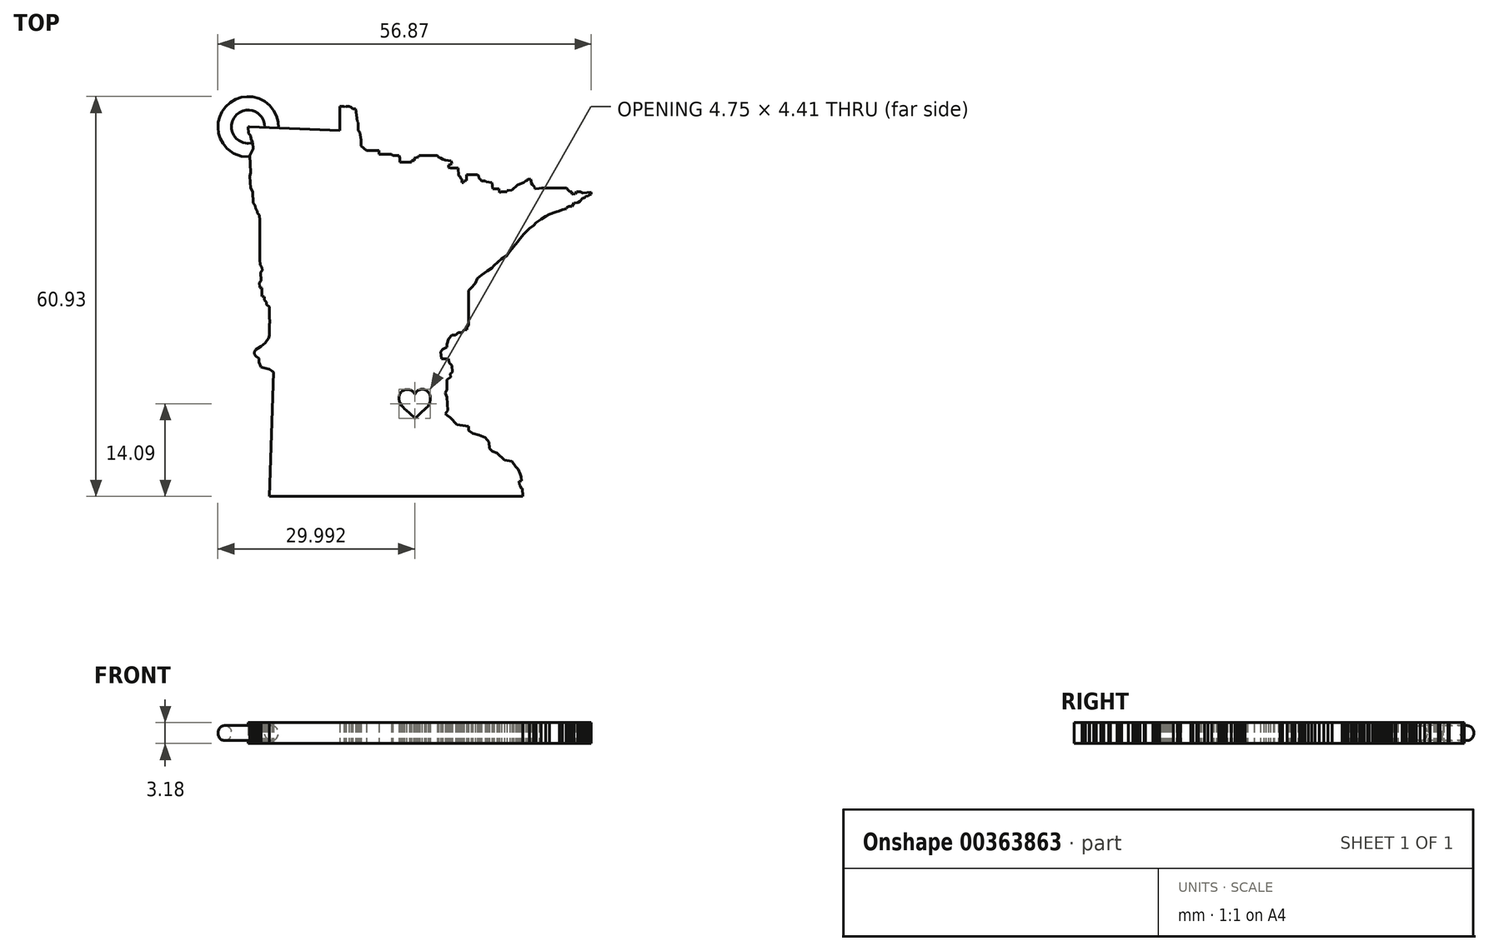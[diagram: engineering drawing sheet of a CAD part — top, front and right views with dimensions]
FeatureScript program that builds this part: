
annotation { "Feature Type Name" : "Feature", "Feature Type Description" : "" }
export const myFeature = defineFeature(function(context is Context, id is Id, definition is map)
    precondition{}
    {
        {
            var Q0;
            Q0=qCreatedBy(makeId("Top.planeOp"),FACE);
            var sketch = newSketch(context, id + "F0", { "sketchPlane" : qUnion([Q0])});
            skLineSegment(sketch, "E0", {"start": v(12.03, -4) * mm, "end": v(25.82, -4.56) * mm});
            skLineSegment(sketch, "E1", {"start": v(25.82, -4.56) * mm, "end": v(25.82, -1.03) * mm});
            skLineSegment(sketch, "E2", {"start": v(25.82, -1.03) * mm, "end": v(25.82, -0.87) * mm});
            skLineSegment(sketch, "E3", {"start": v(25.82, -0.87) * mm, "end": v(26.23, -0.87) * mm});
            skLineSegment(sketch, "E4", {"start": v(26.23, -0.87) * mm, "end": v(26.44, -0.87) * mm});
            skLineSegment(sketch, "E5", {"start": v(26.44, -0.87) * mm, "end": v(26.65, -1.03) * mm});
            skLineSegment(sketch, "E6", {"start": v(26.65, -1.03) * mm, "end": v(26.78, -0.87) * mm});
            skLineSegment(sketch, "E7", {"start": v(26.78, -0.87) * mm, "end": v(27.2, -0.87) * mm});
            skLineSegment(sketch, "E8", {"start": v(27.2, -0.87) * mm, "end": v(27.55, -1.03) * mm});
            skLineSegment(sketch, "E9", {"start": v(27.55, -1.03) * mm, "end": v(27.82, -1.25) * mm});
            skLineSegment(sketch, "E10", {"start": v(27.82, -1.25) * mm, "end": v(28.24, -1.25) * mm});
            skLineSegment(sketch, "E11", {"start": v(28.24, -1.25) * mm, "end": v(28.47, -3.17) * mm});
            skLineSegment(sketch, "E12", {"start": v(28.47, -3.17) * mm, "end": v(28.63, -3.36) * mm});
            skLineSegment(sketch, "E13", {"start": v(28.63, -3.36) * mm, "end": v(28.63, -4.56) * mm});
            skLineSegment(sketch, "E14", {"start": v(28.63, -4.56) * mm, "end": v(28.86, -4.8) * mm});
            skLineSegment(sketch, "E15", {"start": v(28.86, -4.8) * mm, "end": v(29.07, -6.06) * mm});
            skLineSegment(sketch, "E16", {"start": v(29.07, -6.06) * mm, "end": v(29.07, -6.64) * mm});
            skLineSegment(sketch, "E17", {"start": v(29.07, -6.64) * mm, "end": v(29.07, -6.94) * mm});
            skLineSegment(sketch, "E18", {"start": v(29.07, -6.94) * mm, "end": v(29.91, -7.6) * mm});
            skLineSegment(sketch, "E19", {"start": v(29.91, -7.6) * mm, "end": v(31.81, -7.6) * mm});
            skLineSegment(sketch, "E20", {"start": v(31.81, -7.6) * mm, "end": v(31.81, -8.21) * mm});
            skLineSegment(sketch, "E21", {"start": v(31.81, -8.21) * mm, "end": v(33.7, -8.21) * mm});
            skLineSegment(sketch, "E22", {"start": v(33.7, -8.21) * mm, "end": v(33.87, -8.4) * mm});
            skLineSegment(sketch, "E23", {"start": v(33.87, -8.4) * mm, "end": v(34.84, -8.4) * mm});
            skLineSegment(sketch, "E24", {"start": v(34.84, -8.4) * mm, "end": v(35, -8.76) * mm});
            skLineSegment(sketch, "E25", {"start": v(35, -8.76) * mm, "end": v(35, -9.4) * mm});
            skLineSegment(sketch, "E26", {"start": v(35, -9.4) * mm, "end": v(36.75, -9.4) * mm});
            skLineSegment(sketch, "E27", {"start": v(36.75, -9.4) * mm, "end": v(36.75, -9.16) * mm});
            skLineSegment(sketch, "E28", {"start": v(36.75, -9.16) * mm, "end": v(37.17, -9.16) * mm});
            skLineSegment(sketch, "E29", {"start": v(37.17, -9.16) * mm, "end": v(37.17, -8.76) * mm});
            skLineSegment(sketch, "E30", {"start": v(37.17, -8.76) * mm, "end": v(37.77, -8.64) * mm});
            skLineSegment(sketch, "E31", {"start": v(37.77, -8.64) * mm, "end": v(37.9, -8.4) * mm});
            skLineSegment(sketch, "E32", {"start": v(37.9, -8.4) * mm, "end": v(39.55, -8.4) * mm});
            skLineSegment(sketch, "E33", {"start": v(39.55, -8.4) * mm, "end": v(40.68, -8.4) * mm});
            skLineSegment(sketch, "E34", {"start": v(40.68, -8.4) * mm, "end": v(40.9, -8.63) * mm});
            skLineSegment(sketch, "E35", {"start": v(40.9, -8.63) * mm, "end": v(41.2, -8.76) * mm});
            skLineSegment(sketch, "E36", {"start": v(41.2, -8.76) * mm, "end": v(41.49, -8.96) * mm});
            skLineSegment(sketch, "E37", {"start": v(41.49, -8.96) * mm, "end": v(41.87, -9.1) * mm});
            skLineSegment(sketch, "E38", {"start": v(41.87, -9.1) * mm, "end": v(42.76, -9.21) * mm});
            skLineSegment(sketch, "E39", {"start": v(42.76, -9.21) * mm, "end": v(42.9, -9.68) * mm});
            skLineSegment(sketch, "E40", {"start": v(42.9, -9.68) * mm, "end": v(42.4, -9.84) * mm});
            skLineSegment(sketch, "E41", {"start": v(42.4, -9.84) * mm, "end": v(42.4, -10.23) * mm});
            skLineSegment(sketch, "E42", {"start": v(42.4, -10.23) * mm, "end": v(42.7, -10.31) * mm});
            skLineSegment(sketch, "E43", {"start": v(42.7, -10.31) * mm, "end": v(43.03, -10.31) * mm});
            skLineSegment(sketch, "E44", {"start": v(43.03, -10.31) * mm, "end": v(43.87, -10.31) * mm});
            skLineSegment(sketch, "E45", {"start": v(43.87, -10.31) * mm, "end": v(43.95, -11.46) * mm});
            skLineSegment(sketch, "E46", {"start": v(43.95, -11.46) * mm, "end": v(44.17, -11.61) * mm});
            skLineSegment(sketch, "E47", {"start": v(44.17, -11.61) * mm, "end": v(44.27, -11.9) * mm});
            skLineSegment(sketch, "E48", {"start": v(44.27, -11.9) * mm, "end": v(44.43, -12.04) * mm});
            skLineSegment(sketch, "E49", {"start": v(44.43, -12.04) * mm, "end": v(44.46, -12.5) * mm});
            skLineSegment(sketch, "E50", {"start": v(44.46, -12.5) * mm, "end": v(44.7, -12.5) * mm});
            skLineSegment(sketch, "E51", {"start": v(44.7, -12.5) * mm, "end": v(44.77, -12.25) * mm});
            skLineSegment(sketch, "E52", {"start": v(44.77, -12.25) * mm, "end": v(45.11, -12.22) * mm});
            skLineSegment(sketch, "E53", {"start": v(45.11, -12.22) * mm, "end": v(45.11, -11.28) * mm});
            skLineSegment(sketch, "E54", {"start": v(45.11, -11.28) * mm, "end": v(46.8, -11.28) * mm});
            skLineSegment(sketch, "E55", {"start": v(46.8, -11.28) * mm, "end": v(47, -11.44) * mm});
            skLineSegment(sketch, "E56", {"start": v(47, -11.44) * mm, "end": v(47.03, -11.9) * mm});
            skLineSegment(sketch, "E57", {"start": v(47.03, -11.9) * mm, "end": v(47.24, -12.04) * mm});
            skLineSegment(sketch, "E58", {"start": v(47.24, -12.04) * mm, "end": v(47.42, -12.27) * mm});
            skLineSegment(sketch, "E59", {"start": v(47.42, -12.27) * mm, "end": v(47.96, -12.23) * mm});
            skLineSegment(sketch, "E60", {"start": v(47.96, -12.23) * mm, "end": v(48.1, -12.42) * mm});
            skLineSegment(sketch, "E61", {"start": v(48.1, -12.42) * mm, "end": v(48.99, -12.51) * mm});
            skLineSegment(sketch, "E62", {"start": v(48.99, -12.51) * mm, "end": v(49.15, -13.49) * mm});
            skLineSegment(sketch, "E63", {"start": v(49.15, -13.49) * mm, "end": v(50.1, -13.49) * mm});
            skLineSegment(sketch, "E64", {"start": v(50.1, -13.49) * mm, "end": v(50.13, -14.05) * mm});
            skLineSegment(sketch, "E65", {"start": v(50.13, -14.05) * mm, "end": v(50.45, -13.93) * mm});
            skLineSegment(sketch, "E66", {"start": v(50.45, -13.93) * mm, "end": v(51.27, -13.93) * mm});
            skLineSegment(sketch, "E67", {"start": v(51.27, -13.93) * mm, "end": v(51.27, -13.73) * mm});
            skLineSegment(sketch, "E68", {"start": v(51.27, -13.73) * mm, "end": v(52.04, -13.68) * mm});
            skLineSegment(sketch, "E69", {"start": v(52.04, -13.68) * mm, "end": v(52.9, -12.9) * mm});
            skLineSegment(sketch, "E70", {"start": v(52.9, -12.9) * mm, "end": v(53.3, -12.73) * mm});
            skLineSegment(sketch, "E71", {"start": v(53.3, -12.73) * mm, "end": v(53.81, -12.52) * mm});
            skLineSegment(sketch, "E72", {"start": v(53.81, -12.52) * mm, "end": v(54.14, -12.23) * mm});
            skLineSegment(sketch, "E73", {"start": v(54.14, -12.23) * mm, "end": v(54.34, -12.22) * mm});
            skLineSegment(sketch, "E74", {"start": v(54.34, -12.22) * mm, "end": v(54.48, -12.04) * mm});
            skLineSegment(sketch, "E75", {"start": v(54.48, -12.04) * mm, "end": v(54.88, -12) * mm});
            skLineSegment(sketch, "E76", {"start": v(54.88, -12) * mm, "end": v(54.98, -12.23) * mm});
            skLineSegment(sketch, "E77", {"start": v(54.98, -12.23) * mm, "end": v(55, -12.52) * mm});
            skLineSegment(sketch, "E78", {"start": v(55, -12.52) * mm, "end": v(55.15, -12.81) * mm});
            skLineSegment(sketch, "E79", {"start": v(55.15, -12.81) * mm, "end": v(55.37, -13.04) * mm});
            skLineSegment(sketch, "E80", {"start": v(55.37, -13.04) * mm, "end": v(55.52, -13.3) * mm});
            skLineSegment(sketch, "E81", {"start": v(55.52, -13.3) * mm, "end": v(55.53, -13.47) * mm});
            skLineSegment(sketch, "E82", {"start": v(55.53, -13.47) * mm, "end": v(56.2, -13.43) * mm});
            skLineSegment(sketch, "E83", {"start": v(56.2, -13.43) * mm, "end": v(56.59, -13.3) * mm});
            skLineSegment(sketch, "E84", {"start": v(56.59, -13.3) * mm, "end": v(59.44, -13.3) * mm});
            skLineSegment(sketch, "E85", {"start": v(59.44, -13.3) * mm, "end": v(60.4, -13.3) * mm});
            skLineSegment(sketch, "E86", {"start": v(60.4, -13.3) * mm, "end": v(60.62, -13.68) * mm});
            skLineSegment(sketch, "E87", {"start": v(60.62, -13.68) * mm, "end": v(60.85, -13.93) * mm});
            skLineSegment(sketch, "E88", {"start": v(60.85, -13.93) * mm, "end": v(61.17, -13.93) * mm});
            skLineSegment(sketch, "E89", {"start": v(61.17, -13.93) * mm, "end": v(61.2, -14.28) * mm});
            skLineSegment(sketch, "E90", {"start": v(61.2, -14.28) * mm, "end": v(61.68, -14.24) * mm});
            skLineSegment(sketch, "E91", {"start": v(61.68, -14.24) * mm, "end": v(61.91, -13.93) * mm});
            skLineSegment(sketch, "E92", {"start": v(61.91, -13.93) * mm, "end": v(62.46, -13.9) * mm});
            skLineSegment(sketch, "E93", {"start": v(62.46, -13.9) * mm, "end": v(62.85, -14.1) * mm});
            skLineSegment(sketch, "E94", {"start": v(62.85, -14.1) * mm, "end": v(63.82, -14.03) * mm});
            skLineSegment(sketch, "E95", {"start": v(63.82, -14.03) * mm, "end": v(64.1, -14) * mm});
            skLineSegment(sketch, "E96", {"start": v(64.1, -14) * mm, "end": v(64.12, -14.27) * mm});
            skLineSegment(sketch, "E97", {"start": v(64.12, -14.27) * mm, "end": v(63.82, -14.43) * mm});
            skLineSegment(sketch, "E98", {"start": v(63.82, -14.43) * mm, "end": v(63.68, -14.57) * mm});
            skLineSegment(sketch, "E99", {"start": v(63.68, -14.57) * mm, "end": v(63.32, -14.6) * mm});
            skLineSegment(sketch, "E100", {"start": v(63.32, -14.6) * mm, "end": v(63.12, -14.85) * mm});
            skLineSegment(sketch, "E101", {"start": v(63.12, -14.85) * mm, "end": v(62.83, -14.87) * mm});
            skLineSegment(sketch, "E102", {"start": v(62.83, -14.87) * mm, "end": v(62.38, -15.38) * mm});
            skLineSegment(sketch, "E103", {"start": v(62.38, -15.38) * mm, "end": v(62.1, -15.56) * mm});
            skLineSegment(sketch, "E104", {"start": v(62.1, -15.56) * mm, "end": v(61.52, -15.6) * mm});
            skLineSegment(sketch, "E105", {"start": v(61.52, -15.6) * mm, "end": v(61.17, -16.11) * mm});
            skLineSegment(sketch, "E106", {"start": v(61.17, -16.11) * mm, "end": v(60.75, -16.14) * mm});
            skLineSegment(sketch, "E107", {"start": v(60.75, -16.14) * mm, "end": v(60.4, -16.33) * mm});
            skLineSegment(sketch, "E108", {"start": v(60.4, -16.33) * mm, "end": v(60.3, -16.51) * mm});
            skLineSegment(sketch, "E109", {"start": v(60.3, -16.51) * mm, "end": v(59.73, -16.62) * mm});
            skLineSegment(sketch, "E110", {"start": v(59.73, -16.62) * mm, "end": v(59.27, -16.82) * mm});
            skLineSegment(sketch, "E111", {"start": v(59.27, -16.82) * mm, "end": v(58.63, -17.05) * mm});
            skLineSegment(sketch, "E112", {"start": v(58.63, -17.05) * mm, "end": v(57.77, -17.34) * mm});
            skLineSegment(sketch, "E113", {"start": v(57.77, -17.34) * mm, "end": v(57.18, -17.65) * mm});
            skLineSegment(sketch, "E114", {"start": v(57.18, -17.65) * mm, "end": v(56.52, -18.07) * mm});
            skLineSegment(sketch, "E115", {"start": v(56.52, -18.07) * mm, "end": v(55.76, -18.61) * mm});
            skLineSegment(sketch, "E116", {"start": v(55.76, -18.61) * mm, "end": v(55.37, -19.05) * mm});
            skLineSegment(sketch, "E117", {"start": v(55.37, -19.05) * mm, "end": v(54.7, -19.5) * mm});
            skLineSegment(sketch, "E118", {"start": v(54.7, -19.5) * mm, "end": v(53.83, -20.42) * mm});
            skLineSegment(sketch, "E119", {"start": v(53.83, -20.42) * mm, "end": v(53.3, -21) * mm});
            skLineSegment(sketch, "E120", {"start": v(53.3, -21) * mm, "end": v(52.88, -21.62) * mm});
            skLineSegment(sketch, "E121", {"start": v(52.88, -21.62) * mm, "end": v(52.33, -22.3) * mm});
            skLineSegment(sketch, "E122", {"start": v(52.33, -22.3) * mm, "end": v(51.71, -23) * mm});
            skLineSegment(sketch, "E123", {"start": v(51.71, -23) * mm, "end": v(51.27, -23.65) * mm});
            skLineSegment(sketch, "E124", {"start": v(51.27, -23.65) * mm, "end": v(50.45, -24.14) * mm});
            skLineSegment(sketch, "E125", {"start": v(50.45, -24.14) * mm, "end": v(49.9, -24.66) * mm});
            skLineSegment(sketch, "E126", {"start": v(49.9, -24.66) * mm, "end": v(49.31, -25.12) * mm});
            skLineSegment(sketch, "E127", {"start": v(49.31, -25.12) * mm, "end": v(49, -25.55) * mm});
            skLineSegment(sketch, "E128", {"start": v(49, -25.55) * mm, "end": v(48.3, -25.98) * mm});
            skLineSegment(sketch, "E129", {"start": v(48.3, -25.98) * mm, "end": v(47.44, -26.63) * mm});
            skLineSegment(sketch, "E130", {"start": v(47.44, -26.63) * mm, "end": v(46.8, -27.12) * mm});
            skLineSegment(sketch, "E131", {"start": v(46.8, -27.12) * mm, "end": v(46.45, -27.89) * mm});
            skLineSegment(sketch, "E132", {"start": v(46.45, -27.89) * mm, "end": v(45.8, -28.6) * mm});
            skLineSegment(sketch, "E133", {"start": v(45.8, -28.6) * mm, "end": v(45.47, -28.93) * mm});
            skLineSegment(sketch, "E134", {"start": v(45.47, -28.93) * mm, "end": v(45.47, -34.3) * mm});
            skLineSegment(sketch, "E135", {"start": v(45.47, -34.3) * mm, "end": v(45.19, -34.55) * mm});
            skLineSegment(sketch, "E136", {"start": v(45.19, -34.55) * mm, "end": v(45.21, -34.96) * mm});
            skLineSegment(sketch, "E137", {"start": v(45.21, -34.96) * mm, "end": v(44.74, -35) * mm});
            skLineSegment(sketch, "E138", {"start": v(44.74, -35) * mm, "end": v(44.43, -35.36) * mm});
            skLineSegment(sketch, "E139", {"start": v(44.43, -35.36) * mm, "end": v(43.87, -35.4) * mm});
            skLineSegment(sketch, "E140", {"start": v(43.87, -35.4) * mm, "end": v(43.5, -35.74) * mm});
            skLineSegment(sketch, "E141", {"start": v(43.5, -35.74) * mm, "end": v(42.9, -35.78) * mm});
            skLineSegment(sketch, "E142", {"start": v(42.9, -35.78) * mm, "end": v(42.4, -36.35) * mm});
            skLineSegment(sketch, "E143", {"start": v(42.4, -36.35) * mm, "end": v(42.14, -37.13) * mm});
            skLineSegment(sketch, "E144", {"start": v(42.14, -37.13) * mm, "end": v(42.17, -37.61) * mm});
            skLineSegment(sketch, "E145", {"start": v(42.17, -37.61) * mm, "end": v(41.49, -37.93) * mm});
            skLineSegment(sketch, "E146", {"start": v(41.49, -37.93) * mm, "end": v(41.23, -38.3) * mm});
            skLineSegment(sketch, "E147", {"start": v(41.23, -38.3) * mm, "end": v(41.28, -39.01) * mm});
            skLineSegment(sketch, "E148", {"start": v(41.28, -39.01) * mm, "end": v(41.3, -39.4) * mm});
            skLineSegment(sketch, "E149", {"start": v(41.3, -39.4) * mm, "end": v(42.4, -39.4) * mm});
            skLineSegment(sketch, "E150", {"start": v(42.4, -39.4) * mm, "end": v(42.45, -39.96) * mm});
            skLineSegment(sketch, "E151", {"start": v(42.45, -39.96) * mm, "end": v(42.9, -40.42) * mm});
            skLineSegment(sketch, "E152", {"start": v(42.9, -40.42) * mm, "end": v(42.94, -40.94) * mm});
            skLineSegment(sketch, "E153", {"start": v(42.94, -40.94) * mm, "end": v(42.97, -41.41) * mm});
            skLineSegment(sketch, "E154", {"start": v(42.97, -41.41) * mm, "end": v(42.68, -41.63) * mm});
            skLineSegment(sketch, "E155", {"start": v(42.68, -41.63) * mm, "end": v(42.72, -42.2) * mm});
            skLineSegment(sketch, "E156", {"start": v(42.72, -42.2) * mm, "end": v(42.17, -42.55) * mm});
            skLineSegment(sketch, "E157", {"start": v(42.17, -42.55) * mm, "end": v(42.17, -44.1) * mm});
            skLineSegment(sketch, "E158", {"start": v(42.17, -44.1) * mm, "end": v(41.87, -44.55) * mm});
            skLineSegment(sketch, "E159", {"start": v(41.87, -44.55) * mm, "end": v(42.12, -45.2) * mm});
            skLineSegment(sketch, "E160", {"start": v(42.12, -45.2) * mm, "end": v(42.16, -45.83) * mm});
            skLineSegment(sketch, "E161", {"start": v(42.16, -45.83) * mm, "end": v(42.21, -46.63) * mm});
            skLineSegment(sketch, "E162", {"start": v(42.21, -46.63) * mm, "end": v(42.26, -47.28) * mm});
            skLineSegment(sketch, "E163", {"start": v(42.26, -47.28) * mm, "end": v(41.87, -47.75) * mm});
            skLineSegment(sketch, "E164", {"start": v(41.87, -47.75) * mm, "end": v(42.21, -48.03) * mm});
            skLineSegment(sketch, "E165", {"start": v(42.21, -48.03) * mm, "end": v(42.64, -48.3) * mm});
            skLineSegment(sketch, "E166", {"start": v(42.64, -48.3) * mm, "end": v(43.67, -49.43) * mm});
            skLineSegment(sketch, "E167", {"start": v(43.67, -49.43) * mm, "end": v(45.42, -49.65) * mm});
            skLineSegment(sketch, "E168", {"start": v(45.42, -49.65) * mm, "end": v(45.46, -50.3) * mm});
            skLineSegment(sketch, "E169", {"start": v(45.46, -50.3) * mm, "end": v(46.1, -50.73) * mm});
            skLineSegment(sketch, "E170", {"start": v(46.1, -50.73) * mm, "end": v(47.01, -51) * mm});
            skLineSegment(sketch, "E171", {"start": v(47.01, -51) * mm, "end": v(47.96, -51.4) * mm});
            skLineSegment(sketch, "E172", {"start": v(47.96, -51.4) * mm, "end": v(48.56, -52.06) * mm});
            skLineSegment(sketch, "E173", {"start": v(48.56, -52.06) * mm, "end": v(48.6, -52.65) * mm});
            skLineSegment(sketch, "E174", {"start": v(48.6, -52.65) * mm, "end": v(48.63, -53.05) * mm});
            skLineSegment(sketch, "E175", {"start": v(48.63, -53.05) * mm, "end": v(49.09, -53.47) * mm});
            skLineSegment(sketch, "E176", {"start": v(49.09, -53.47) * mm, "end": v(49.8, -53.75) * mm});
            skLineSegment(sketch, "E177", {"start": v(49.8, -53.75) * mm, "end": v(50.92, -54.8) * mm});
            skLineSegment(sketch, "E178", {"start": v(50.92, -54.8) * mm, "end": v(52.04, -55.02) * mm});
            skLineSegment(sketch, "E179", {"start": v(52.04, -55.02) * mm, "end": v(52.64, -55.8) * mm});
            skLineSegment(sketch, "E180", {"start": v(52.64, -55.8) * mm, "end": v(53, -56.22) * mm});
            skLineSegment(sketch, "E181", {"start": v(53, -56.22) * mm, "end": v(53.3, -56.98) * mm});
            skLineSegment(sketch, "E182", {"start": v(53.3, -56.98) * mm, "end": v(53.47, -57.32) * mm});
            skLineSegment(sketch, "E183", {"start": v(53.47, -57.32) * mm, "end": v(53.51, -58) * mm});
            skLineSegment(sketch, "E184", {"start": v(53.51, -58) * mm, "end": v(53.14, -58.02) * mm});
            skLineSegment(sketch, "E185", {"start": v(53.14, -58.02) * mm, "end": v(53.18, -58.58) * mm});
            skLineSegment(sketch, "E186", {"start": v(53.18, -58.58) * mm, "end": v(53.3, -58.76) * mm});
            skLineSegment(sketch, "E187", {"start": v(53.3, -58.76) * mm, "end": v(53.49, -59.18) * mm});
            skLineSegment(sketch, "E188", {"start": v(53.49, -59.18) * mm, "end": v(53.62, -59.11) * mm});
            skLineSegment(sketch, "E189", {"start": v(53.62, -59.11) * mm, "end": v(53.69, -60.12) * mm});
            skLineSegment(sketch, "E190", {"start": v(53.69, -60.12) * mm, "end": v(53.7, -60.33) * mm});
            skLineSegment(sketch, "E191", {"start": v(53.7, -60.33) * mm, "end": v(15.07, -60.33) * mm});
            skLineSegment(sketch, "E192", {"start": v(15.07, -60.33) * mm, "end": v(15.7, -41.41) * mm});
            skLineSegment(sketch, "E193", {"start": v(15.7, -41.41) * mm, "end": v(15.5, -41.2) * mm});
            skLineSegment(sketch, "E194", {"start": v(15.5, -41.2) * mm, "end": v(15.08, -40.95) * mm});
            skLineSegment(sketch, "E195", {"start": v(15.08, -40.95) * mm, "end": v(14.34, -40.76) * mm});
            skLineSegment(sketch, "E196", {"start": v(14.34, -40.76) * mm, "end": v(13.8, -40.62) * mm});
            skLineSegment(sketch, "E197", {"start": v(13.8, -40.62) * mm, "end": v(13.52, -39.9) * mm});
            skLineSegment(sketch, "E198", {"start": v(13.52, -39.9) * mm, "end": v(13.5, -39.58) * mm});
            skLineSegment(sketch, "E199", {"start": v(13.5, -39.58) * mm, "end": v(13.48, -39.31) * mm});
            skLineSegment(sketch, "E200", {"start": v(13.48, -39.31) * mm, "end": v(13.1, -39.01) * mm});
            skLineSegment(sketch, "E201", {"start": v(13.1, -39.01) * mm, "end": v(12.84, -38.69) * mm});
            skLineSegment(sketch, "E202", {"start": v(12.84, -38.69) * mm, "end": v(12.81, -38.33) * mm});
            skLineSegment(sketch, "E203", {"start": v(12.81, -38.33) * mm, "end": v(13.03, -37.99) * mm});
            skLineSegment(sketch, "E204", {"start": v(13.03, -37.99) * mm, "end": v(13.32, -37.77) * mm});
            skLineSegment(sketch, "E205", {"start": v(13.32, -37.77) * mm, "end": v(13.84, -37.46) * mm});
            skLineSegment(sketch, "E206", {"start": v(13.84, -37.46) * mm, "end": v(14.14, -37.2) * mm});
            skLineSegment(sketch, "E207", {"start": v(14.14, -37.2) * mm, "end": v(14.47, -36.94) * mm});
            skLineSegment(sketch, "E208", {"start": v(14.47, -36.94) * mm, "end": v(14.7, -36.58) * mm});
            skLineSegment(sketch, "E209", {"start": v(14.7, -36.58) * mm, "end": v(14.99, -36.24) * mm});
            skLineSegment(sketch, "E210", {"start": v(14.99, -36.24) * mm, "end": v(15.1, -35.82) * mm});
            skLineSegment(sketch, "E211", {"start": v(15.1, -35.82) * mm, "end": v(15.1, -34.13) * mm});
            skLineSegment(sketch, "E212", {"start": v(15.1, -34.13) * mm, "end": v(15.16, -33.88) * mm});
            skLineSegment(sketch, "E213", {"start": v(15.16, -33.88) * mm, "end": v(15.15, -33.7) * mm});
            skLineSegment(sketch, "E214", {"start": v(15.15, -33.7) * mm, "end": v(15.12, -33.3) * mm});
            skLineSegment(sketch, "E215", {"start": v(15.12, -33.3) * mm, "end": v(15.1, -32.89) * mm});
            skLineSegment(sketch, "E216", {"start": v(15.1, -32.89) * mm, "end": v(15.1, -31.93) * mm});
            skLineSegment(sketch, "E217", {"start": v(15.1, -31.93) * mm, "end": v(15.06, -31.43) * mm});
            skLineSegment(sketch, "E218", {"start": v(15.06, -31.43) * mm, "end": v(14.66, -31.12) * mm});
            skLineSegment(sketch, "E219", {"start": v(14.66, -31.12) * mm, "end": v(14.63, -30.73) * mm});
            skLineSegment(sketch, "E220", {"start": v(14.63, -30.73) * mm, "end": v(14.34, -30.4) * mm});
            skLineSegment(sketch, "E221", {"start": v(14.34, -30.4) * mm, "end": v(14.31, -29.94) * mm});
            skLineSegment(sketch, "E222", {"start": v(14.31, -29.94) * mm, "end": v(13.97, -29.85) * mm});
            skLineSegment(sketch, "E223", {"start": v(13.97, -29.85) * mm, "end": v(13.97, -29.2) * mm});
            skLineSegment(sketch, "E224", {"start": v(13.97, -29.2) * mm, "end": v(13.93, -28.6) * mm});
            skLineSegment(sketch, "E225", {"start": v(13.93, -28.6) * mm, "end": v(13.65, -28.52) * mm});
            skLineSegment(sketch, "E226", {"start": v(13.65, -28.52) * mm, "end": v(13.6, -27.74) * mm});
            skLineSegment(sketch, "E227", {"start": v(13.6, -27.74) * mm, "end": v(13.83, -27.5) * mm});
            skLineSegment(sketch, "E228", {"start": v(13.83, -27.5) * mm, "end": v(13.8, -27) * mm});
            skLineSegment(sketch, "E229", {"start": v(13.8, -27) * mm, "end": v(13.74, -26.2) * mm});
            skLineSegment(sketch, "E230", {"start": v(13.74, -26.2) * mm, "end": v(14, -25.9) * mm});
            skLineSegment(sketch, "E231", {"start": v(14, -25.9) * mm, "end": v(13.97, -25.38) * mm});
            skLineSegment(sketch, "E232", {"start": v(13.97, -25.38) * mm, "end": v(13.69, -25.06) * mm});
            skLineSegment(sketch, "E233", {"start": v(13.69, -25.06) * mm, "end": v(13.63, -24.19) * mm});
            skLineSegment(sketch, "E234", {"start": v(13.63, -24.19) * mm, "end": v(13.63, -19.05) * mm});
            skLineSegment(sketch, "E235", {"start": v(13.63, -19.05) * mm, "end": v(13.63, -18.3) * mm});
            skLineSegment(sketch, "E236", {"start": v(13.63, -18.3) * mm, "end": v(13.59, -17.68) * mm});
            skLineSegment(sketch, "E237", {"start": v(13.59, -17.68) * mm, "end": v(13.57, -17.47) * mm});
            skLineSegment(sketch, "E238", {"start": v(13.57, -17.47) * mm, "end": v(13.26, -17.18) * mm});
            skLineSegment(sketch, "E239", {"start": v(13.26, -17.18) * mm, "end": v(13.24, -16.83) * mm});
            skLineSegment(sketch, "E240", {"start": v(13.24, -16.83) * mm, "end": v(13, -16.5) * mm});
            skLineSegment(sketch, "E241", {"start": v(13, -16.5) * mm, "end": v(12.97, -16.03) * mm});
            skLineSegment(sketch, "E242", {"start": v(12.97, -16.03) * mm, "end": v(12.64, -15.62) * mm});
            skLineSegment(sketch, "E243", {"start": v(12.64, -15.62) * mm, "end": v(12.62, -15.24) * mm});
            skLineSegment(sketch, "E244", {"start": v(12.62, -15.24) * mm, "end": v(12.6, -15.03) * mm});
            skLineSegment(sketch, "E245", {"start": v(12.6, -15.03) * mm, "end": v(12.57, -14.6) * mm});
            skLineSegment(sketch, "E246", {"start": v(12.57, -14.6) * mm, "end": v(12.53, -13.93) * mm});
            skLineSegment(sketch, "E247", {"start": v(12.53, -13.93) * mm, "end": v(12.22, -13.3) * mm});
            skLineSegment(sketch, "E248", {"start": v(12.22, -13.3) * mm, "end": v(12.19, -12.73) * mm});
            skLineSegment(sketch, "E249", {"start": v(12.19, -12.73) * mm, "end": v(12.14, -12.04) * mm});
            skLineSegment(sketch, "E250", {"start": v(12.14, -12.04) * mm, "end": v(12.1, -11.57) * mm});
            skLineSegment(sketch, "E251", {"start": v(12.1, -11.57) * mm, "end": v(12.26, -10.98) * mm});
            skLineSegment(sketch, "E252", {"start": v(12.26, -10.98) * mm, "end": v(12.23, -10.59) * mm});
            skLineSegment(sketch, "E253", {"start": v(12.23, -10.59) * mm, "end": v(12.22, -10.31) * mm});
            skLineSegment(sketch, "E254", {"start": v(12.22, -10.31) * mm, "end": v(12.17, -9.68) * mm});
            skLineSegment(sketch, "E255", {"start": v(12.17, -9.68) * mm, "end": v(12.09, -8.4) * mm});
            skLineSegment(sketch, "E256", {"start": v(12.09, -8.4) * mm, "end": v(12.62, -7.4) * mm});
            skLineSegment(sketch, "E257", {"start": v(12.62, -7.4) * mm, "end": v(12.55, -6.4) * mm});
            skLineSegment(sketch, "E258", {"start": v(12.55, -6.4) * mm, "end": v(12.34, -6.13) * mm});
            skLineSegment(sketch, "E259", {"start": v(12.34, -6.13) * mm, "end": v(12.23, -5.5) * mm});
            skLineSegment(sketch, "E260", {"start": v(12.23, -5.5) * mm, "end": v(12.23, -5.34) * mm});
            skLineSegment(sketch, "E261", {"start": v(12.23, -5.34) * mm, "end": v(12.12, -5.2) * mm});
            skLineSegment(sketch, "E262", {"start": v(12.12, -5.2) * mm, "end": v(11.93, -5.03) * mm});
            skLineSegment(sketch, "E263", {"start": v(11.93, -5.03) * mm, "end": v(11.86, -4) * mm});
            skLineSegment(sketch, "E264", {"start": v(11.86, -4) * mm, "end": v(12.03, -4) * mm});
            skSolve(sketch);
        }
        {
            var Q0;
            Q0 = qSketchRegion(id + "F0", true);
            extrude(context, id + "F1", {"entities" : qUnion([Q0]), "depth" : 3.17 * mm});
        }
        {
            var Q0;
            Q0=qCreatedBy(makeId("Front.planeOp"),FACE);
            cPlane(context, id + "F2", {"entities" : qUnion([Q0]), "cplaneType" : CPlaneType.OFFSET, "offset" : 2.54 * mm, "width" : 152.4 * mm, "height" : 152.4 * mm});
        }
        {
            var Q0;
            Q0=qCreatedBy(id+"F2.planeOp",FACE);
            var sketch = newSketch(context, id + "F3", { "sketchPlane" : qUnion([Q0])});
            skCircle(sketch, "E265", {"center": v(15.08, 1.59) * mm, "radius": 1.14 * mm});
            skSolve(sketch);
        }
        {
            var Q0;
            Q0 = qSketchRegion(id + "F3", true);
            var Q1;
            Q1=makeQuery(id+"F1.opExtrude","SWEPT_EDGE",EDGE,{"disambiguationData":[OSD([sQuery(id+"F0.wireOp",EDGE,"E263"),sQuery(id+"F0.wireOp",EDGE,"E264")])]});
            revolve(context, id + "F4", {"operationType" : NewBodyOperationType.ADD, "entities" : qUnion([Q0]), "axis" : qUnion([Q1]), "revolveType" : RevolveType.FULL});
        }
        {
            var Q0;
            Q0=qCreatedBy(makeId("Top.planeOp"),FACE);
            var sketch = newSketch(context, id + "F5", { "sketchPlane" : qUnion([Q0])});
            skArc(sketch, "E266", {"start": v(37.26, -44.78) * mm, "mid": v(35.77, -44.1) * mm, "end": v(34.87, -45.46) * mm});
            skArc(sketch, "E267", {"start": v(39.6, -45.25) * mm, "mid": v(38.62, -44.04) * mm, "end": v(37.26, -44.78) * mm});
            skLineSegment(sketch, "E268", {"start": v(34.87, -45.46) * mm, "end": v(34.92, -45.9) * mm});
            skLineSegment(sketch, "E269", {"start": v(34.92, -45.9) * mm, "end": v(35.04, -46.19) * mm});
            skLineSegment(sketch, "E270", {"start": v(35.04, -46.19) * mm, "end": v(35.2, -46.48) * mm});
            skLineSegment(sketch, "E271", {"start": v(35.2, -46.48) * mm, "end": v(35.46, -46.77) * mm});
            skLineSegment(sketch, "E272", {"start": v(35.46, -46.77) * mm, "end": v(35.68, -47) * mm});
            skLineSegment(sketch, "E273", {"start": v(35.68, -47) * mm, "end": v(35.97, -47.27) * mm});
            skLineSegment(sketch, "E274", {"start": v(35.97, -47.27) * mm, "end": v(36.42, -47.64) * mm});
            skLineSegment(sketch, "E275", {"start": v(36.42, -47.64) * mm, "end": v(36.66, -47.87) * mm});
            skLineSegment(sketch, "E276", {"start": v(36.66, -47.87) * mm, "end": v(37.04, -48.18) * mm});
            skLineSegment(sketch, "E277", {"start": v(37.04, -48.18) * mm, "end": v(37.25, -48.45) * mm});
            skLineSegment(sketch, "E278", {"start": v(37.25, -48.45) * mm, "end": v(37.48, -48.26) * mm});
            skLineSegment(sketch, "E279", {"start": v(37.48, -48.26) * mm, "end": v(37.76, -48) * mm});
            skLineSegment(sketch, "E280", {"start": v(37.76, -48) * mm, "end": v(38.04, -47.73) * mm});
            skLineSegment(sketch, "E281", {"start": v(38.04, -47.73) * mm, "end": v(38.36, -47.46) * mm});
            skLineSegment(sketch, "E282", {"start": v(38.36, -47.46) * mm, "end": v(38.7, -47.15) * mm});
            skLineSegment(sketch, "E283", {"start": v(38.7, -47.15) * mm, "end": v(38.99, -46.88) * mm});
            skLineSegment(sketch, "E284", {"start": v(38.99, -46.88) * mm, "end": v(39.26, -46.6) * mm});
            skLineSegment(sketch, "E285", {"start": v(39.26, -46.6) * mm, "end": v(39.43, -46.32) * mm});
            skLineSegment(sketch, "E286", {"start": v(39.43, -46.32) * mm, "end": v(39.55, -46.04) * mm});
            skLineSegment(sketch, "E287", {"start": v(39.55, -46.04) * mm, "end": v(39.62, -45.68) * mm});
            skLineSegment(sketch, "E288", {"start": v(39.62, -45.68) * mm, "end": v(39.62, -45.58) * mm});
            skLineSegment(sketch, "E289", {"start": v(39.62, -45.58) * mm, "end": v(39.6, -45.25) * mm});
            skSolve(sketch);
        }
        {
            var Q0;
            Q0=makeQuery(id+"F5.imprint","IMPRINT",FACE,{"disambiguationData":[TD([[makeQuery(id+"F5.imprint","IMPRINT",EDGE,{"derivedFrom":sQuery(id+"F5.wireOp",EDGE,"E266")}),1.0]])]});
            extrude(context, id + "F6", {"entities" : qUnion([Q0]), "operationType" : NewBodyOperationType.REMOVE, "depth" : 3.17 * mm});
        }
    });
